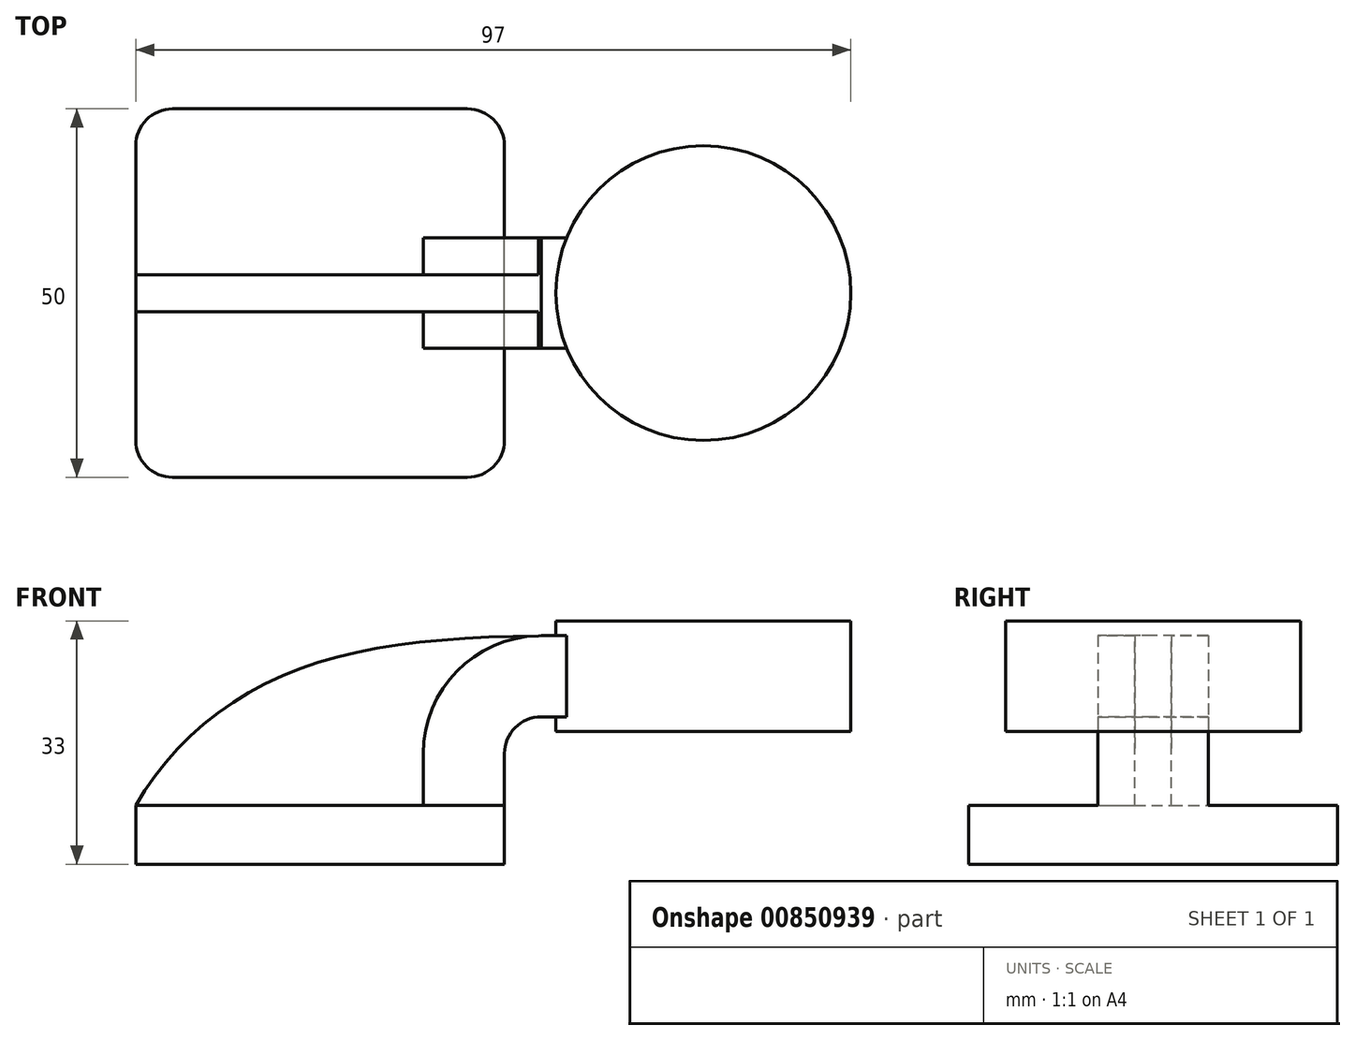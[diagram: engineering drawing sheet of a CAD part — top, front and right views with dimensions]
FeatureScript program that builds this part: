
annotation { "Feature Type Name" : "Feature", "Feature Type Description" : "" }
export const myFeature = defineFeature(function(context is Context, id is Id, definition is map)
    precondition{}
    {
        {
            var Q0;
            Q0=qCreatedBy(makeId("Front.planeOp"),FACE);
            var sketch = newSketch(context, id + "F0", { "sketchPlane" : qUnion([Q0])});
            skLineSegment(sketch, "E0.bottom", {"start": v(25, -4) * mm, "end": v(-25, -4) * mm});
            skLineSegment(sketch, "E0.top", {"start": v(25, 4) * mm, "end": v(-25, 4) * mm});
            skLineSegment(sketch, "E0.left", {"start": v(25, -4) * mm, "end": v(25, 4) * mm});
            skLineSegment(sketch, "E0.right", {"start": v(-25, -4) * mm, "end": v(-25, 4) * mm});
            skPoint(sketch, "E0.middle", {"position": v(0, 0) * mm});
            skLineSegment(sketch, "E1.bottom", {"start": v(32, 14) * mm, "end": v(72, 14) * mm});
            skLineSegment(sketch, "E1.top", {"start": v(32, 29) * mm, "end": v(72, 29) * mm});
            skLineSegment(sketch, "E1.left", {"start": v(32, 14) * mm, "end": v(32, 29) * mm});
            skLineSegment(sketch, "E1.right", {"start": v(72, 14) * mm, "end": v(72, 29) * mm});
            skPoint(sketch, "E1.middle", {"position": v(52, 21.5) * mm});
            skLineSegment(sketch, "E2", {"start": v(25, 4) * mm, "end": v(25, 11) * mm});
            skArc(sketch, "E3", {"start": v(25, 11) * mm, "mid": v(26.46, 14.54) * mm, "end": v(30, 16) * mm});
            skLineSegment(sketch, "E4", {"start": v(30, 16) * mm, "end": v(52, 16) * mm});
            skLineSegment(sketch, "E5.0", {"start": v(30, 27) * mm, "end": v(52, 27) * mm});
            skArc(sketch, "E5.1", {"start": v(14, 11) * mm, "mid": v(18.69, 22.31) * mm, "end": v(30, 27) * mm});
            skLineSegment(sketch, "E5.2", {"start": v(14, 4) * mm, "end": v(14, 11) * mm});
            skFitSpline(sketch, "E6", {"points": [v(-25, 4) * mm, v(-6.37, 21.01) * mm, v(30, 27) * mm], "startDerivative": vector(26.93, 47.28) * mm, "endDerivative": vector(80.54, 0.91) * mm});
            skLineSegment(sketch, "E7", {"start": v(52, 11.5) * mm, "end": v(52, 31.5) * mm});
            skSolve(sketch);
        }
        {
            var Q0;
            Q0=makeQuery(id+"F0.imprint","IMPRINT",FACE,{"disambiguationData":[TD([[makeQuery(id+"F0.imprint","IMPRINT",EDGE,{"derivedFrom":sQuery(id+"F0.wireOp",EDGE,"E0.bottom")}),-1.0]])]});
            extrude(context, id + "F1", {"entities" : qUnion([Q0]), "depth" : 50 * mm, "offsetDistance" : 25 * mm, "symmetric" : true});
        }
        {
            var Q0;
            {var subQ1=sQuery(id+"F0.wireOp",EDGE,"E2");Q0=makeQuery(id+"F0.imprint","IMPRINT",FACE,{"disambiguationData":[TD([[makeQuery(id+"F0.imprint","IMPRINT",EDGE,{"derivedFrom":subQ1}),1.0]])]});}
            var Q1;
            {var subQ0=sQuery(id+"F0.wireOp",EDGE,"E4");var subQ1=sQuery(id+"F0.wireOp",EDGE,"E1.left");var subQ2=makeQuery(id+"F0.imprint","INTERSECT",VERTEX,{"derivedFrom":[subQ1,subQ0]});Q1=makeQuery(id+"F0.imprint","IMPRINT",FACE,{"disambiguationData":[TD([[makeQuery(id+"F0.imprint","IMPRINT",EDGE,{"disambiguationData":[TD([[subQ2,-1.0]])],"derivedFrom":subQ1}),-1.0]])]});}
            extrude(context, id + "F2", {"entities" : qUnion([Q0, Q1]), "operationType" : NewBodyOperationType.ADD, "depth" : 15 * mm, "offsetDistance" : 25 * mm, "symmetric" : true});
        }
        {
            var Q0;
            {var subQ3=sQuery(id+"F0.wireOp",EDGE,"E5.2");Q0=makeQuery(id+"F0.imprint","IMPRINT",FACE,{"disambiguationData":[TD([[makeQuery(id+"F0.imprint","IMPRINT",EDGE,{"derivedFrom":subQ3}),1.0]])]});}
            extrude(context, id + "F3", {"entities" : qUnion([Q0]), "operationType" : NewBodyOperationType.ADD, "depth" : 5 * mm, "offsetDistance" : 25 * mm, "symmetric" : true});
        }
        {
            var Q0;
            {var subQ4=sQuery(id+"F0.wireOp",EDGE,"E1.right");Q0=makeQuery(id+"F0.imprint","IMPRINT",FACE,{"disambiguationData":[TD([[makeQuery(id+"F0.imprint","IMPRINT",EDGE,{"derivedFrom":subQ4}),1.0]])]});}
            var Q1;
            Q1=sQuery(id+"F0.wireOp",EDGE,"E7");
            revolve(context, id + "F4", {"operationType" : NewBodyOperationType.ADD, "surfaceOperationType" : NewSurfaceOperationType.NEW, "entities" : qUnion([Q0]), "axis" : qUnion([Q1]), "revolveType" : RevolveType.FULL});
        }
        {
            var Q0;
            Q0=makeQuery(id+"F1.opExtrude","CAP_EDGE",EDGE,{"disambiguationData":[OSD([sQuery(id+"F0.wireOp",EDGE,"E0.left")])],"isStart":true});
            var Q1;
            Q1=makeQuery(id+"F1.opExtrude","CAP_EDGE",EDGE,{"disambiguationData":[OSD([sQuery(id+"F0.wireOp",EDGE,"E0.right")])],"isStart":true});
            var Q2;
            Q2=makeQuery(id+"F1.opExtrude","CAP_EDGE",EDGE,{"disambiguationData":[OSD([sQuery(id+"F0.wireOp",EDGE,"E0.right")])],"isStart":false});
            var Q3;
            Q3=makeQuery(id+"F1.opExtrude","CAP_EDGE",EDGE,{"disambiguationData":[OSD([sQuery(id+"F0.wireOp",EDGE,"E0.left")])],"isStart":false});
            fillet(context, id + "F5", {"entities" : qUnion([Q0, Q1, Q2, Q3]), "radius" : 5 * mm, "allowEdgeOverflow" : false});
        }
    });
